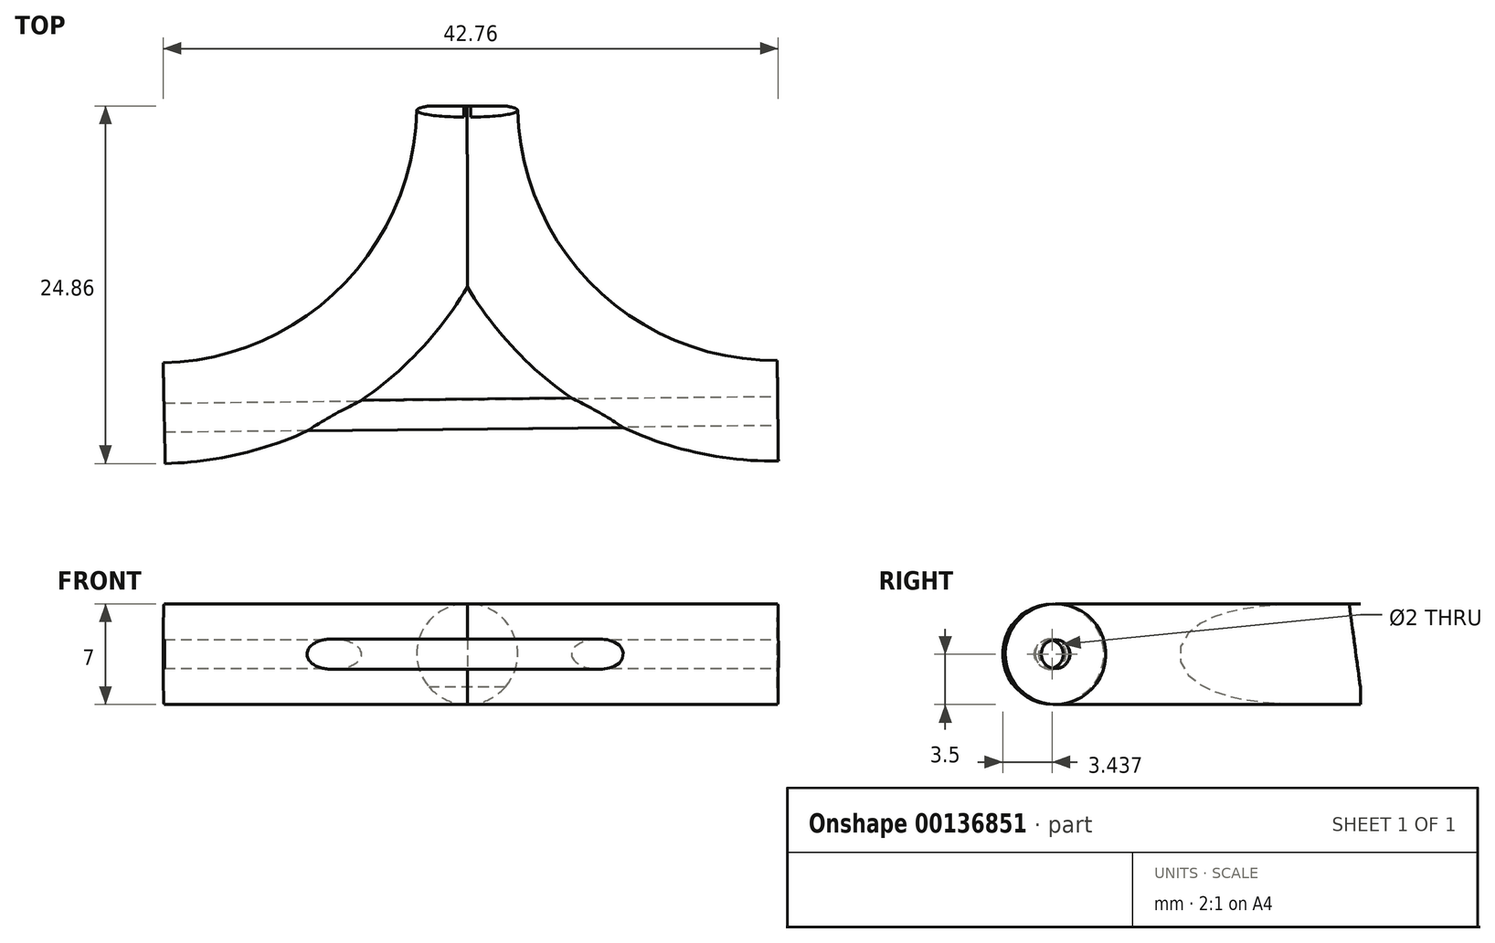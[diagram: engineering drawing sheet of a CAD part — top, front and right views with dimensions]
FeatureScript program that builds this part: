
annotation { "Feature Type Name" : "Feature", "Feature Type Description" : "" }
export const myFeature = defineFeature(function(context is Context, id is Id, definition is map)
    precondition{}
    {
        {
            var Q0;
            Q0=qCreatedBy(makeId("Front.planeOp"),FACE);
            var sketch = newSketch(context, id + "F0", { "sketchPlane" : qUnion([Q0])});
            skPoint(sketch, "E0.start.orphan", {"position": v(4.05, 0) * mm});
            skCircle(sketch, "E1", {"center": v(0, 0) * mm, "radius": 3.5 * mm});
            skPoint(sketch, "E2.start.orphan", {"position": v(-3.5, 0) * mm});
            skLineSegment(sketch, "E3", {"start": v(3.5, 0) * mm, "end": v(-3.5, 0) * mm});
            skSolve(sketch);
        }
        {
            var Q0;
            Q0=qCreatedBy(makeId("Top.planeOp"),FACE);
            var sketch = newSketch(context, id + "F1", { "sketchPlane" : qUnion([Q0])});
            skPoint(sketch, "E4.first.point", {"position": v(0, 0) * mm});
            skPoint(sketch, "E4.second.point", {"position": v(0, 0) * mm});
            skPoint(sketch, "E4.third.point", {"position": v(0.4, 0.02) * mm});
            skArc(sketch, "E5", {"start": v(-21.06, -21.52) * mm, "mid": v(-6.14, -15.05) * mm, "end": v(0, 0) * mm});
            skPoint(sketch, "E5.second.point", {"position": v(-43.04, 0) * mm});
            skPoint(sketch, "E5.third.point", {"position": v(-21.06, -21.52) * mm});
            skArc(sketch, "E6", {"start": v(0, 0) * mm, "mid": v(6.34, -15.18) * mm, "end": v(21.59, -21.35) * mm});
            skPoint(sketch, "E6.second.point", {"position": v(42.7, 0.02) * mm});
            skPoint(sketch, "E6.third.point", {"position": v(21.59, -21.35) * mm});
            skSolve(sketch);
        }
        {
            var Q0;
            {var subQ0=sQuery(id+"F0.wireOp",EDGE,"E3");Q0=makeQuery(id+"F0.imprint","IMPRINT",FACE,{"disambiguationData":[TD([[makeQuery(id+"F0.imprint","IMPRINT",EDGE,{"derivedFrom":subQ0}),-1.0]])]});}
            var Q1;
            {var subQ0=sQuery(id+"F0.wireOp",EDGE,"E3");Q1=makeQuery(id+"F0.imprint","IMPRINT",FACE,{"disambiguationData":[TD([[makeQuery(id+"F0.imprint","IMPRINT",EDGE,{"derivedFrom":subQ0}),1.0]])]});}
            var Q2;
            Q2=sQuery(id+"F1.wireOp",EDGE,"E6");
            sweep(context, id + "F2", {"profiles" : qUnion([Q0, Q1]), "path" : qUnion([Q2])});
        }
        {
            var Q0;
            Q0=qCreatedBy(makeId("Right.planeOp"),FACE);
            var sketch = newSketch(context, id + "F3", { "sketchPlane" : qUnion([Q0])});
            skCircle(sketch, "E7", {"center": v(-21.35, 0) * mm, "radius": 1 * mm});
            skLineSegment(sketch, "E8", {"start": v(0, -3.5) * mm, "end": v(-0.94, 3.5) * mm});
            skLineSegment(sketch, "E9", {"start": v(-0.94, 3.5) * mm, "end": v(0, 3.5) * mm});
            skLineSegment(sketch, "E10", {"start": v(0, 3.5) * mm, "end": v(0, -3.5) * mm});
            skSolve(sketch);
        }
        {
            var Q0;
            {var subQ0=sQuery(id+"F0.wireOp",EDGE,"E3");Q0=makeQuery(id+"F0.imprint","IMPRINT",FACE,{"disambiguationData":[TD([[makeQuery(id+"F0.imprint","IMPRINT",EDGE,{"derivedFrom":subQ0}),1.0]])]});}
            var Q1;
            {var subQ0=sQuery(id+"F0.wireOp",EDGE,"E3");Q1=makeQuery(id+"F0.imprint","IMPRINT",FACE,{"disambiguationData":[TD([[makeQuery(id+"F0.imprint","IMPRINT",EDGE,{"derivedFrom":subQ0}),-1.0]])]});}
            var Q2;
            Q2=sQuery(id+"F1.wireOp",EDGE,"E5");
            sweep(context, id + "F4", {"operationType" : NewBodyOperationType.ADD, "profiles" : qUnion([Q0, Q1]), "path" : qUnion([Q2])});
        }
        {
            var Q0;
            Q0=makeQuery(id+"F2.opSweep","CAP_FACE",FACE,{"disambiguationData":[OSD([sQuery(id+"F0.wireOp",EDGE,"E1"),sQuery(id+"F1.wireOp",VERTEX,"E6.end")])],"isStart":false});
            var sketch = newSketch(context, id + "F5", { "sketchPlane" : qUnion([Q0])});
            skCircle(sketch, "E11", {"center": v(-21.59, 0) * mm, "radius": 1.05 * mm});
            skCircle(sketch, "E12", {"center": v(-21.59, 0) * mm, "radius": 1 * mm});
            skSolve(sketch);
        }
        {
            var Q0;
            Q0=makeQuery(id+"F5.imprint","IMPRINT",FACE,{"disambiguationData":[TD([[makeQuery(id+"F5.imprint","IMPRINT",EDGE,{"derivedFrom":sQuery(id+"F5.wireOp",EDGE,"E11")}),1.0]])]});
            extrude(context, id + "F6", {"entities" : qUnion([Q0]), "operationType" : NewBodyOperationType.ADD, "oppositeDirection" : true, "depth" : 42.45 * mm});
        }
        {
            var Q0;
            Q0=makeQuery(id+"F5.imprint","IMPRINT",FACE,{"disambiguationData":[TD([[makeQuery(id+"F5.imprint","IMPRINT",EDGE,{"derivedFrom":sQuery(id+"F5.wireOp",EDGE,"E12")}),1.0]])]});
            var Q1;
            Q1=makeQuery(id+"F4.opSweep","CAP_FACE",FACE,{"disambiguationData":[OSD([sQuery(id+"F0.wireOp",EDGE,"E1"),sQuery(id+"F1.wireOp",VERTEX,"E5.start")])],"isStart":false});
            extrude(context, id + "F7", {"entities" : qUnion([Q0, Q1]), "operationType" : NewBodyOperationType.REMOVE, "oppositeDirection" : true, "depth" : 42.9 * mm});
        }
        {
            var Q0;
            {var subQ0=sQuery(id+"F0.wireOp",EDGE,"E3");Q0=makeQuery(id+"F0.imprint","IMPRINT",FACE,{"disambiguationData":[TD([[makeQuery(id+"F0.imprint","IMPRINT",EDGE,{"derivedFrom":subQ0}),1.0]])]});}
            var sketch = newSketch(context, id + "F8", { "sketchPlane" : qUnion([Q0])});
            skCircle(sketch, "E13", {"center": v(0, 0) * mm, "radius": 3.5 * mm});
            skSolve(sketch);
        }
        {
            var Q0;
            Q0 = qSketchRegion(id + "F8", true);
            extrude(context, id + "F9", {"entities" : qUnion([Q0]), "operationType" : NewBodyOperationType.REMOVE, "depth" : 0.16 * mm});
        }
        {
            var Q0;
            Q0=makeQuery(id+"F3.imprint","IMPRINT",FACE,{"disambiguationData":[TD([[makeQuery(id+"F3.imprint","IMPRINT",EDGE,{"derivedFrom":sQuery(id+"F3.wireOp",EDGE,"E8")}),-1.0]])]});
            extrude(context, id + "F10", {"entities" : qUnion([Q0]), "operationType" : NewBodyOperationType.REMOVE, "oppositeDirection" : true, "depth" : 7.75 * mm, "symmetric" : true});
        }
    });
